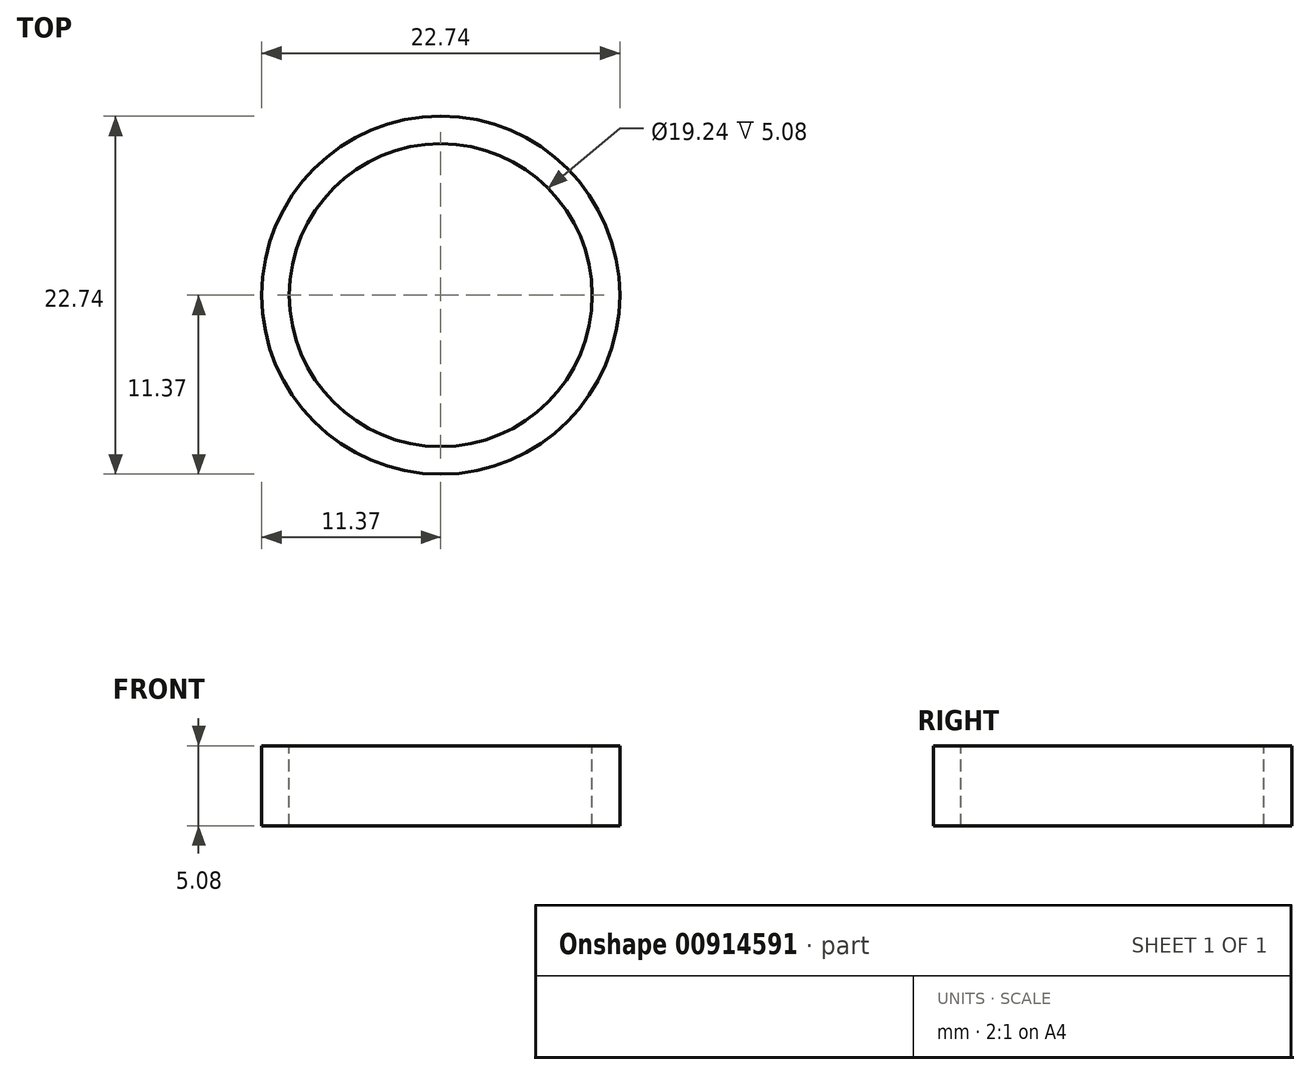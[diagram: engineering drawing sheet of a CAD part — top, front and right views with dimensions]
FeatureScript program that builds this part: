
annotation { "Feature Type Name" : "Feature", "Feature Type Description" : "" }
export const myFeature = defineFeature(function(context is Context, id is Id, definition is map)
    precondition{}
    {
        {
            var Q0;
            Q0=qCreatedBy(makeId("Right.planeOp"),FACE);
            var sketch = newSketch(context, id + "F0", { "sketchPlane" : qUnion([Q0])});
            skLineSegment(sketch, "E0", {"start": v(0, 5.08) * mm, "end": v(0, 0) * mm});
            skLineSegment(sketch, "E1", {"start": v(0, 5.08) * mm, "end": v(11.37, 5.08) * mm});
            skLineSegment(sketch, "E2", {"start": v(11.37, 5.08) * mm, "end": v(11.37, 0) * mm});
            skLineSegment(sketch, "E3", {"start": v(11.37, 0) * mm, "end": v(0, 0) * mm});
            skSolve(sketch);
        }
        {
            var Q0;
            Q0=makeQuery(id+"F0.imprint","IMPRINT",FACE,{"disambiguationData":[TD([[makeQuery(id+"F0.imprint","IMPRINT",EDGE,{"derivedFrom":sQuery(id+"F0.wireOp",EDGE,"E0")}),1.0]])]});
            var Q1;
            Q1=sQuery(id+"F0.wireOp",EDGE,"E0");
            revolve(context, id + "F1", {"surfaceOperationType" : NewSurfaceOperationType.NEW, "entities" : qUnion([Q0]), "axis" : qUnion([Q1]), "revolveType" : RevolveType.FULL});
        }
        {
            var Q0;
            Q0=makeQuery(id+"F1.opRevolve","SWEPT_FACE",FACE,{"disambiguationData":[OSD([sQuery(id+"F0.wireOp",EDGE,"E1")])]});
            var Q1;
            Q1=makeQuery(id+"F1.opRevolve","SWEPT_FACE",FACE,{"disambiguationData":[OSD([sQuery(id+"F0.wireOp",EDGE,"E3")])]});
            shell(context, id + "F2", {"entities" : qUnion([Q0, Q1]), "thickness" : 1.75 * mm});
        }
    });
